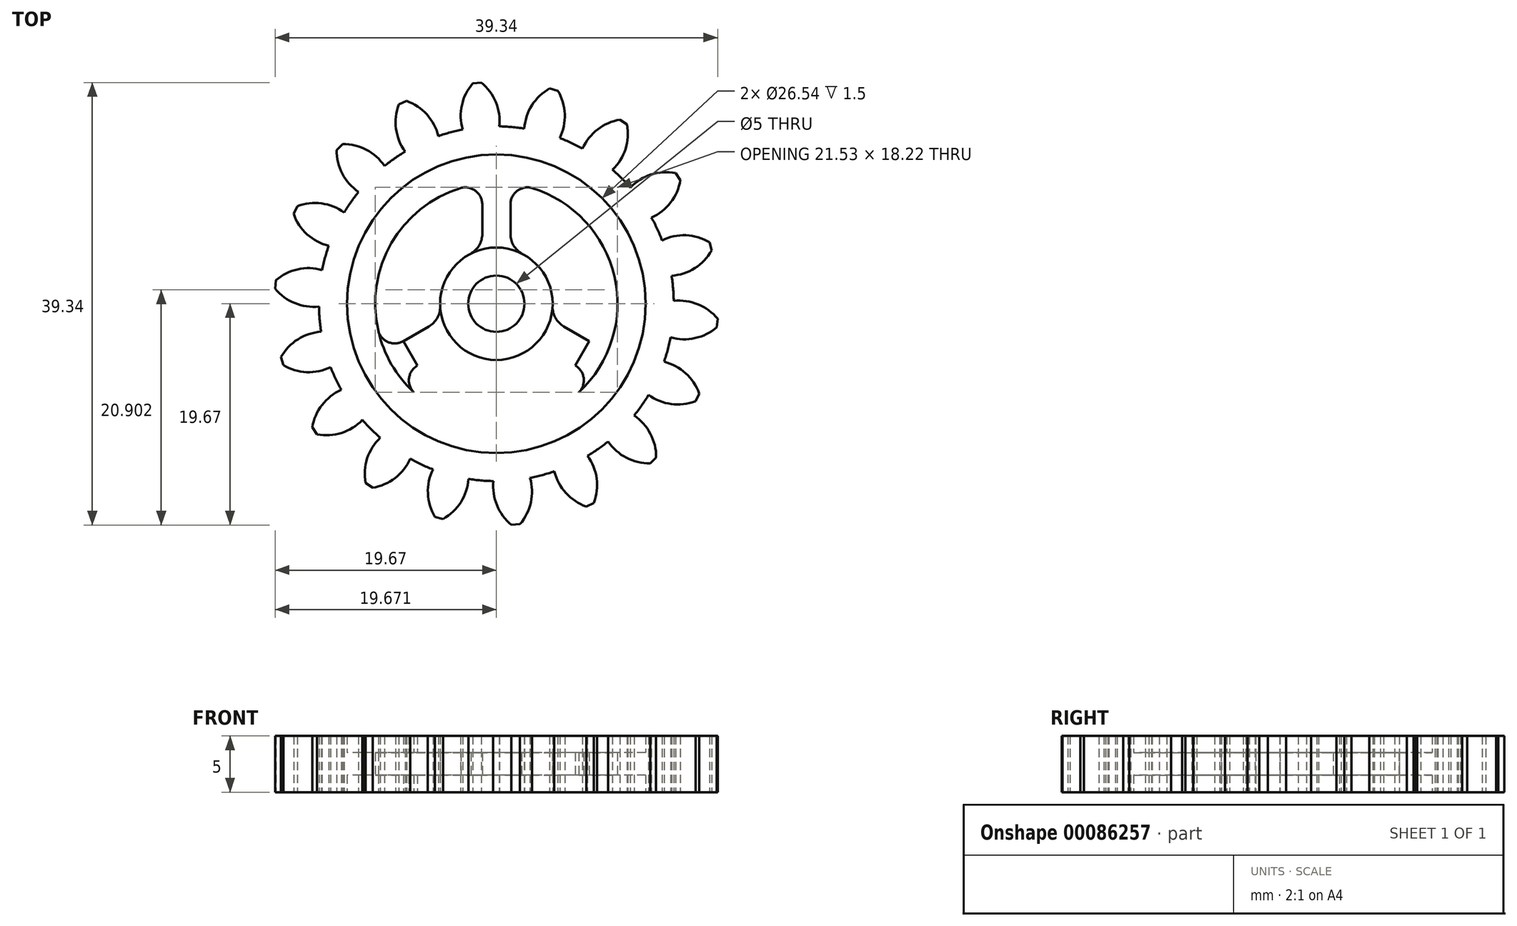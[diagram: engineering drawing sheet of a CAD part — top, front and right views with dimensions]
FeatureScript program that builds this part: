
annotation { "Feature Type Name" : "Feature", "Feature Type Description" : "" }
export const myFeature = defineFeature(function(context is Context, id is Id, definition is map)
    precondition{}
    {
        {
            assignVariable(context, id + "F0", {"name" : "Teeth", "anyValue" : 18});
        }
        {
            assignVariable(context, id + "F1", {"name" : "GearDepth", "anyValue" : 5});
        }
        {
            var Q0;
            Q0=qCreatedBy(makeId("Top.planeOp"),FACE);
            var sketch = newSketch(context, id + "F2", { "sketchPlane" : qUnion([Q0])});
            skCircle(sketch, "E0", {"center": v(0, 0) * mm, "radius": 15.77 * mm});
            skCircle(sketch, "E1", {"center": v(0, 0) * mm, "radius": 17.74 * mm, "construction": true});
            skCircle(sketch, "E2", {"center": v(0, 0) * mm, "radius": 19.71 * mm, "construction": true});
            skLineSegment(sketch, "E3", {"start": v(0, 0) * mm, "end": v(0, 17.6) * mm, "construction": true});
            skLineSegment(sketch, "E4", {"start": v(0, 0) * mm, "end": v(-1.57, 17.98) * mm, "construction": true});
            skLineSegment(sketch, "E5", {"start": v(0, 17.74) * mm, "end": v(-10.54, 17.74) * mm, "construction": true});
            skLineSegment(sketch, "E6", {"start": v(0, 17.74) * mm, "end": v(-10.3, 14) * mm, "construction": true});
            skCircle(sketch, "E7", {"center": v(0, 17.74) * mm, "radius": 4.44 * mm, "construction": true});
            skCircle(sketch, "E8", {"center": v(-4.17, 16.22) * mm, "radius": 4.44 * mm, "construction": true});
            skArc(sketch, "E9", {"start": v(-8.34, 17.74) * mm, "mid": v(-0.03, 14.63) * mm, "end": v(-8.28, 17.89) * mm, "construction": true});
            skArc(sketch, "E10.trimOffspring", {"start": v(0.26, 15.77) * mm, "mid": v(-0.05, 17.92) * mm, "end": v(-1.34, 19.67) * mm});
            skArc(sketch, "E11.MirrorCS", {"start": v(-3, 15.48) * mm, "mid": v(-3.06, 17.66) * mm, "end": v(-2.1, 19.6) * mm});
            skLineSegment(sketch, "E12", {"start": v(-2.1, 19.6) * mm, "end": v(-1.34, 19.67) * mm});
            skLineSegment(sketch, "E13.19.1", {"start": v(4.07, 19.29) * mm, "end": v(4.8, 19.12) * mm});
            skCircle(sketch, "E14", {"center": v(0, 0) * mm, "radius": 2.5 * mm});
            skSolve(sketch);
        }
        {
            var Q0;
            Q0=qCreatedBy(makeId("Front.planeOp"),FACE);
            var sketch = newSketch(context, id + "F3", { "sketchPlane" : qUnion([Q0])});
            skLineSegment(sketch, "E15", {"start": v(0, 0) * mm, "end": v(0, 61.57) * mm});
            skSolve(sketch);
        }
        {
            var Q0;
            {var subQ0=sQuery(id+"F2.wireOp",EDGE,"E10.trimOffspring");Q0=makeQuery(id+"F2.imprint","IMPRINT",FACE,{"disambiguationData":[TD([[makeQuery(id+"F2.imprint","IMPRINT",EDGE,{"derivedFrom":subQ0}),1.0]])]});}
            var Q1;
            {var subQ0=sQuery(id+"F2.wireOp",EDGE,"E0");var subQ1=makeQuery(id+"F2.imprint","INTERSECT",VERTEX,{"derivedFrom":[subQ0,sQuery(id+"F2.wireOp",EDGE,"E10.trimOffspring")]});Q1=makeQuery(id+"F2.imprint","IMPRINT",FACE,{"disambiguationData":[TD([[makeQuery(id+"F2.imprint","IMPRINT",EDGE,{"disambiguationData":[TD([[subQ1,-1.0]])],"derivedFrom":subQ0}),1.0]])]});}
            var Q2;
            {var subQ0=sQuery(id+"F2.wireOp",EDGE,"E13.1.0");Q2=makeQuery(id+"F2.imprint","IMPRINT",FACE,{"disambiguationData":[TD([[makeQuery(id+"F2.imprint","IMPRINT",EDGE,{"derivedFrom":subQ0}),1.0]])]});}
            var Q3;
            {var subQ0=sQuery(id+"F2.wireOp",EDGE,"E13.2.0");Q3=makeQuery(id+"F2.imprint","IMPRINT",FACE,{"disambiguationData":[TD([[makeQuery(id+"F2.imprint","IMPRINT",EDGE,{"derivedFrom":subQ0}),1.0]])]});}
            var Q4;
            {var subQ0=sQuery(id+"F2.wireOp",EDGE,"E13.3.0");Q4=makeQuery(id+"F2.imprint","IMPRINT",FACE,{"disambiguationData":[TD([[makeQuery(id+"F2.imprint","IMPRINT",EDGE,{"derivedFrom":subQ0}),1.0]])]});}
            var Q5;
            {var subQ0=sQuery(id+"F2.wireOp",EDGE,"E13.4.0");Q5=makeQuery(id+"F2.imprint","IMPRINT",FACE,{"disambiguationData":[TD([[makeQuery(id+"F2.imprint","IMPRINT",EDGE,{"derivedFrom":subQ0}),1.0]])]});}
            var Q6;
            {var subQ0=sQuery(id+"F2.wireOp",EDGE,"E13.5.0");Q6=makeQuery(id+"F2.imprint","IMPRINT",FACE,{"disambiguationData":[TD([[makeQuery(id+"F2.imprint","IMPRINT",EDGE,{"derivedFrom":subQ0}),1.0]])]});}
            var Q7;
            {var subQ0=sQuery(id+"F2.wireOp",EDGE,"E13.6.0");Q7=makeQuery(id+"F2.imprint","IMPRINT",FACE,{"disambiguationData":[TD([[makeQuery(id+"F2.imprint","IMPRINT",EDGE,{"derivedFrom":subQ0}),1.0]])]});}
            var Q8;
            {var subQ0=sQuery(id+"F2.wireOp",EDGE,"E13.7.0");Q8=makeQuery(id+"F2.imprint","IMPRINT",FACE,{"disambiguationData":[TD([[makeQuery(id+"F2.imprint","IMPRINT",EDGE,{"derivedFrom":subQ0}),1.0]])]});}
            var Q9;
            {var subQ0=sQuery(id+"F2.wireOp",EDGE,"E13.8.0");Q9=makeQuery(id+"F2.imprint","IMPRINT",FACE,{"disambiguationData":[TD([[makeQuery(id+"F2.imprint","IMPRINT",EDGE,{"derivedFrom":subQ0}),1.0]])]});}
            var Q10;
            {var subQ0=sQuery(id+"F2.wireOp",EDGE,"E13.9.0");Q10=makeQuery(id+"F2.imprint","IMPRINT",FACE,{"disambiguationData":[TD([[makeQuery(id+"F2.imprint","IMPRINT",EDGE,{"derivedFrom":subQ0}),1.0]])]});}
            var Q11;
            {var subQ0=sQuery(id+"F2.wireOp",EDGE,"E13.10.0");Q11=makeQuery(id+"F2.imprint","IMPRINT",FACE,{"disambiguationData":[TD([[makeQuery(id+"F2.imprint","IMPRINT",EDGE,{"derivedFrom":subQ0}),1.0]])]});}
            var Q12;
            {var subQ0=sQuery(id+"F2.wireOp",EDGE,"E13.11.0");Q12=makeQuery(id+"F2.imprint","IMPRINT",FACE,{"disambiguationData":[TD([[makeQuery(id+"F2.imprint","IMPRINT",EDGE,{"derivedFrom":subQ0}),1.0]])]});}
            var Q13;
            {var subQ0=sQuery(id+"F2.wireOp",EDGE,"E13.12.0");Q13=makeQuery(id+"F2.imprint","IMPRINT",FACE,{"disambiguationData":[TD([[makeQuery(id+"F2.imprint","IMPRINT",EDGE,{"derivedFrom":subQ0}),1.0]])]});}
            var Q14;
            {var subQ0=sQuery(id+"F2.wireOp",EDGE,"E13.13.0");Q14=makeQuery(id+"F2.imprint","IMPRINT",FACE,{"disambiguationData":[TD([[makeQuery(id+"F2.imprint","IMPRINT",EDGE,{"derivedFrom":subQ0}),1.0]])]});}
            var Q15;
            {var subQ0=sQuery(id+"F2.wireOp",EDGE,"E13.14.0");Q15=makeQuery(id+"F2.imprint","IMPRINT",FACE,{"disambiguationData":[TD([[makeQuery(id+"F2.imprint","IMPRINT",EDGE,{"derivedFrom":subQ0}),1.0]])]});}
            var Q16;
            {var subQ0=sQuery(id+"F2.wireOp",EDGE,"E13.15.0");Q16=makeQuery(id+"F2.imprint","IMPRINT",FACE,{"disambiguationData":[TD([[makeQuery(id+"F2.imprint","IMPRINT",EDGE,{"derivedFrom":subQ0}),1.0]])]});}
            var Q17;
            {var subQ0=sQuery(id+"F2.wireOp",EDGE,"E13.16.0");Q17=makeQuery(id+"F2.imprint","IMPRINT",FACE,{"disambiguationData":[TD([[makeQuery(id+"F2.imprint","IMPRINT",EDGE,{"derivedFrom":subQ0}),1.0]])]});}
            var Q18;
            {var subQ0=sQuery(id+"F2.wireOp",EDGE,"E13.17.0");Q18=makeQuery(id+"F2.imprint","IMPRINT",FACE,{"disambiguationData":[TD([[makeQuery(id+"F2.imprint","IMPRINT",EDGE,{"derivedFrom":subQ0}),1.0]])]});}
            var Q19;
            {var subQ0=sQuery(id+"F2.wireOp",EDGE,"E13.18.0");Q19=makeQuery(id+"F2.imprint","IMPRINT",FACE,{"disambiguationData":[TD([[makeQuery(id+"F2.imprint","IMPRINT",EDGE,{"derivedFrom":subQ0}),1.0]])]});}
            var Q20;
            {var subQ0=sQuery(id+"F2.wireOp",EDGE,"E13.19.0");Q20=makeQuery(id+"F2.imprint","IMPRINT",FACE,{"disambiguationData":[TD([[makeQuery(id+"F2.imprint","IMPRINT",EDGE,{"derivedFrom":subQ0}),1.0]])]});}
            var Q21;
            Q21=sQuery(id+"F2.wireOp",EDGE,"E0");
            var Q22;
            Q22=sQuery(id+"F2.wireOp",EDGE,"E10.trimOffspring");
            var Q23;
            Q23=sQuery(id+"F2.wireOp",EDGE,"E12");
            var Q24;
            Q24=sQuery(id+"F2.wireOp",EDGE,"E11.MirrorCS");
            extrude(context, id + "F4", {"entities" : qUnion([Q0, Q1, Q2, Q3, Q4, Q5, Q6, Q7, Q8, Q9, Q10, Q11, Q12, Q13, Q14, Q15, Q16, Q17, Q18, Q19, Q20]), "surfaceEntities" : qUnion([Q21, Q22, Q23, Q24]), "depth" : (getVariable(context, 'GearDepth')) * mm});
        }
        {
            var Q0;
            Q0=makeQuery(id+"F4.opExtrude","SWEPT_BODY",BODY,{"disambiguationData":[OSD([sQuery(id+"F2.wireOp",EDGE,"E0"),sQuery(id+"F2.wireOp",EDGE,"E10.trimOffspring"),sQuery(id+"F2.wireOp",EDGE,"E11.MirrorCS"),sQuery(id+"F2.wireOp",EDGE,"E12"),sQuery(id+"F2.wireOp",EDGE,"E14")])]});
            var Q1;
            Q1=sQuery(id+"F3.wireOp",EDGE,"E15");
            circularPattern(context, id + "F5", {"operationType" : NewBodyOperationType.ADD, "entities" : qUnion([Q0]), "axis" : qUnion([Q1]), "angle" : (360 / getVariable(context, 'Teeth')) * degree, "instanceCount" : getVariable(context, 'Teeth')});
        }
        {
            var Q0;
            Q0=qCreatedBy(makeId("Top.planeOp"),FACE);
            var sketch = newSketch(context, id + "F6", { "sketchPlane" : qUnion([Q0])});
            skCircle(sketch, "E16", {"center": v(0, 0) * mm, "radius": 5 * mm});
            skCircle(sketch, "E17", {"center": v(0, 0) * mm, "radius": 13.27 * mm});
            skLineSegment(sketch, "E18.bottom", {"start": v(-1.25, 8.82) * mm, "end": v(1.25, 8.82) * mm});
            skLineSegment(sketch, "E18.top", {"start": v(-1.25, 6.2) * mm, "end": v(1.25, 6.2) * mm});
            skLineSegment(sketch, "E18.left", {"start": v(-1.25, 8.82) * mm, "end": v(-1.25, 6.2) * mm});
            skLineSegment(sketch, "E18.right", {"start": v(1.25, 8.82) * mm, "end": v(1.25, 6.2) * mm});
            skLineSegment(sketch, "E19", {"start": v(0, 0) * mm, "end": v(0, 14.95) * mm, "construction": true});
            skArc(sketch, "E20", {"start": v(1.25, 6.2) * mm, "mid": v(1.52, 5.2) * mm, "end": v(2.26, 4.46) * mm});
            skArc(sketch, "E21.MirrorCS", {"start": v(-1.25, 6.2) * mm, "mid": v(-1.52, 5.2) * mm, "end": v(-2.26, 4.46) * mm});
            skCircle(sketch, "E22", {"center": v(0, 0) * mm, "radius": 10.77 * mm});
            skArc(sketch, "E23", {"start": v(-1.25, 8.82) * mm, "mid": v(-1.84, 10.02) * mm, "end": v(-3.15, 10.3) * mm});
            skArc(sketch, "E24.MirrorCS", {"start": v(1.25, 8.82) * mm, "mid": v(1.84, 10.02) * mm, "end": v(3.15, 10.3) * mm});
            skArc(sketch, "E25.1.0", {"start": v(7.01, -5.5) * mm, "mid": v(7.76, -6.6) * mm, "end": v(7.34, -7.88) * mm});
            skArc(sketch, "E25.1.1", {"start": v(8.26, -3.33) * mm, "mid": v(9.6, -3.42) * mm, "end": v(10.5, -2.42) * mm});
            skLineSegment(sketch, "E25.1.2", {"start": v(8.26, -3.33) * mm, "end": v(7.01, -5.5) * mm});
            skLineSegment(sketch, "E25.1.3", {"start": v(8.26, -3.33) * mm, "end": v(6, -2.02) * mm});
            skLineSegment(sketch, "E25.1.4", {"start": v(7.01, -5.5) * mm, "end": v(4.74, -4.18) * mm});
            skLineSegment(sketch, "E25.1.5", {"start": v(6, -2.02) * mm, "end": v(4.74, -4.18) * mm});
            skArc(sketch, "E25.1.6", {"start": v(4.74, -4.18) * mm, "mid": v(3.74, -3.91) * mm, "end": v(2.73, -4.19) * mm});
            skArc(sketch, "E25.1.7", {"start": v(6, -2.02) * mm, "mid": v(5.26, -1.28) * mm, "end": v(5, -0.27) * mm});
            skArc(sketch, "E25.2.0", {"start": v(-8.26, -3.33) * mm, "mid": v(-9.6, -3.42) * mm, "end": v(-10.5, -2.42) * mm});
            skArc(sketch, "E25.2.1", {"start": v(-7.01, -5.5) * mm, "mid": v(-7.76, -6.6) * mm, "end": v(-7.34, -7.88) * mm});
            skLineSegment(sketch, "E25.2.2", {"start": v(-7.01, -5.5) * mm, "end": v(-8.26, -3.33) * mm});
            skLineSegment(sketch, "E25.2.3", {"start": v(-7.01, -5.5) * mm, "end": v(-4.74, -4.18) * mm});
            skLineSegment(sketch, "E25.2.4", {"start": v(-8.26, -3.33) * mm, "end": v(-6, -2.02) * mm});
            skLineSegment(sketch, "E25.2.5", {"start": v(-4.74, -4.18) * mm, "end": v(-6, -2.02) * mm});
            skArc(sketch, "E25.2.6", {"start": v(-6, -2.02) * mm, "mid": v(-5.26, -1.28) * mm, "end": v(-5, -0.27) * mm});
            skArc(sketch, "E25.2.7", {"start": v(-4.74, -4.18) * mm, "mid": v(-3.74, -3.91) * mm, "end": v(-2.73, -4.19) * mm});
            skLineSegment(sketch, "E25.anchor1", {"start": v(0, 0) * mm, "end": v(1.25, 8.82) * mm, "construction": true});
            skLineSegment(sketch, "E25.anchor2", {"start": v(0, 0) * mm, "end": v(-8.26, -3.33) * mm, "construction": true});
            skSolve(sketch);
        }
        {
            var Q0;
            Q0=makeQuery(id+"F6.imprint","IMPRINT",FACE,{"disambiguationData":[TD([[makeQuery(id+"F6.imprint","IMPRINT",EDGE,{"derivedFrom":sQuery(id+"F6.wireOp",EDGE,"E18.right")}),1.0]])]});
            var Q1;
            Q1=makeQuery(id+"F6.imprint","IMPRINT",FACE,{"disambiguationData":[TD([[makeQuery(id+"F6.imprint","IMPRINT",EDGE,{"derivedFrom":sQuery(id+"F6.wireOp",EDGE,"E18.left")}),-1.0]])]});
            var Q2;
            {var subQ0=sQuery(id+"F6.wireOp",EDGE,"275d905c-acd0-4467-9c6b-4b6f0fef50b3.1.1");Q2=makeQuery(id+"F6.imprint","IMPRINT",FACE,{"disambiguationData":[TD([[makeQuery(id+"F6.imprint","IMPRINT",EDGE,{"derivedFrom":subQ0}),1.0]])]});}
            extrude(context, id + "F7", {"entities" : qUnion([Q0, Q1, Q2]), "operationType" : NewBodyOperationType.REMOVE, "endBound" : BoundingType.THROUGH_ALL, "depth" : 25 * mm});
        }
        {
            var Q0;
            Q0=makeQuery(id+"F6.imprint","IMPRINT",FACE,{"disambiguationData":[TD([[makeQuery(id+"F6.imprint","IMPRINT",EDGE,{"derivedFrom":sQuery(id+"F6.wireOp",EDGE,"E17")}),1.0]])]});
            var Q1;
            {var subQ0=sQuery(id+"F6.wireOp",EDGE,"E16");var subQ5=makeQuery(id+"F6.imprint","INTERSECT",VERTEX,{"derivedFrom":[subQ0,sQuery(id+"F6.wireOp",EDGE,"E20")]});Q1=makeQuery(id+"F6.imprint","IMPRINT",FACE,{"disambiguationData":[TD([[makeQuery(id+"F6.imprint","IMPRINT",EDGE,{"disambiguationData":[TD([[subQ5,-1.0]])],"derivedFrom":subQ0}),1.0]])]});}
            var Q2;
            Q2=makeQuery(id+"F6.imprint","IMPRINT",FACE,{"disambiguationData":[TD([[makeQuery(id+"F6.imprint","IMPRINT",EDGE,{"derivedFrom":sQuery(id+"F6.wireOp",EDGE,"E18.top")}),-1.0]])]});
            var Q3;
            Q3=makeQuery(id+"F6.imprint","IMPRINT",FACE,{"disambiguationData":[TD([[makeQuery(id+"F6.imprint","IMPRINT",EDGE,{"derivedFrom":sQuery(id+"F6.wireOp",EDGE,"E18.bottom")}),-1.0]])]});
            var Q4;
            Q4=makeQuery(id+"F6.imprint","IMPRINT",FACE,{"disambiguationData":[TD([[makeQuery(id+"F6.imprint","IMPRINT",EDGE,{"derivedFrom":sQuery(id+"F6.wireOp",EDGE,"E18.bottom")}),1.0]])]});
            var Q5;
            Q5=makeQuery(id+"F6.imprint","IMPRINT",FACE,{"disambiguationData":[TD([[makeQuery(id+"F6.imprint","IMPRINT",EDGE,{"derivedFrom":sQuery(id+"F6.wireOp",EDGE,"E25.2.5")}),-1.0]])]});
            var Q6;
            Q6=makeQuery(id+"F6.imprint","IMPRINT",FACE,{"disambiguationData":[TD([[makeQuery(id+"F6.imprint","IMPRINT",EDGE,{"derivedFrom":sQuery(id+"F6.wireOp",EDGE,"E25.2.2")}),-1.0]])]});
            var Q7;
            {var subQ0=sQuery(id+"F6.wireOp",EDGE,"E25.2.0");Q7=makeQuery(id+"F6.imprint","IMPRINT",FACE,{"disambiguationData":[TD([[makeQuery(id+"F6.imprint","IMPRINT",EDGE,{"derivedFrom":subQ0}),1.0]])]});}
            var Q8;
            {var subQ0=sQuery(id+"F6.wireOp",EDGE,"E25.1.0");Q8=makeQuery(id+"F6.imprint","IMPRINT",FACE,{"disambiguationData":[TD([[makeQuery(id+"F6.imprint","IMPRINT",EDGE,{"derivedFrom":subQ0}),1.0]])]});}
            var Q9;
            Q9=makeQuery(id+"F6.imprint","IMPRINT",FACE,{"disambiguationData":[TD([[makeQuery(id+"F6.imprint","IMPRINT",EDGE,{"derivedFrom":sQuery(id+"F6.wireOp",EDGE,"E25.1.2")}),-1.0]])]});
            var Q10;
            Q10=makeQuery(id+"F6.imprint","IMPRINT",FACE,{"disambiguationData":[TD([[makeQuery(id+"F6.imprint","IMPRINT",EDGE,{"derivedFrom":sQuery(id+"F6.wireOp",EDGE,"E25.1.5")}),-1.0]])]});
            extrude(context, id + "F8", {"entities" : qUnion([Q0, Q1, Q2, Q3, Q4, Q5, Q6, Q7, Q8, Q9, Q10]), "operationType" : NewBodyOperationType.REMOVE, "depth" : 1.5 * mm});
        }
        {
            var Q0;
            {var subQ0=sQuery(id+"F6.wireOp",EDGE,"E25.1.0");var subQ6=makeQuery(id+"F4.opExtrude","CAP_FACE",FACE,{"disambiguationData":[OSD([sQuery(id+"F2.wireOp",EDGE,"E0"),sQuery(id+"F2.wireOp",EDGE,"E10.trimOffspring"),sQuery(id+"F2.wireOp",EDGE,"E11.MirrorCS"),sQuery(id+"F2.wireOp",EDGE,"E12"),sQuery(id+"F2.wireOp",EDGE,"E14")])],"isStart":true});Q0=makeQuery(id+"F8.boolean.opBoolean","SPLIT",FACE,{"disambiguationData":[TD([makeQuery(id+"F8.opExtrude","SWEPT_FACE",FACE,{"disambiguationData":[OSD([subQ0])]})])],"derivedFrom":makeQuery(id+"F5.boolean.opBoolean","MERGE",FACE,{"derivedFrom":[subQ6,makeQuery(id+"F5.opPattern","COPY",FACE,{"derivedFrom":subQ6,"instanceName":"1"}),makeQuery(id+"F5.opPattern","COPY",FACE,{"derivedFrom":subQ6,"instanceName":"2"}),makeQuery(id+"F5.opPattern","COPY",FACE,{"derivedFrom":subQ6,"instanceName":"3"}),makeQuery(id+"F5.opPattern","COPY",FACE,{"derivedFrom":subQ6,"instanceName":"4"}),makeQuery(id+"F5.opPattern","COPY",FACE,{"derivedFrom":subQ6,"instanceName":"5"}),makeQuery(id+"F5.opPattern","COPY",FACE,{"derivedFrom":subQ6,"instanceName":"6"}),makeQuery(id+"F5.opPattern","COPY",FACE,{"derivedFrom":subQ6,"instanceName":"7"}),makeQuery(id+"F5.opPattern","COPY",FACE,{"derivedFrom":subQ6,"instanceName":"8"}),makeQuery(id+"F5.opPattern","COPY",FACE,{"derivedFrom":subQ6,"instanceName":"9"}),makeQuery(id+"F5.opPattern","COPY",FACE,{"derivedFrom":subQ6,"instanceName":"10"}),makeQuery(id+"F5.opPattern","COPY",FACE,{"derivedFrom":subQ6,"instanceName":"11"}),makeQuery(id+"F5.opPattern","COPY",FACE,{"derivedFrom":subQ6,"instanceName":"12"}),makeQuery(id+"F5.opPattern","COPY",FACE,{"derivedFrom":subQ6,"instanceName":"13"}),makeQuery(id+"F5.opPattern","COPY",FACE,{"derivedFrom":subQ6,"instanceName":"14"}),makeQuery(id+"F5.opPattern","COPY",FACE,{"derivedFrom":subQ6,"instanceName":"15"}),makeQuery(id+"F5.opPattern","COPY",FACE,{"derivedFrom":subQ6,"instanceName":"16"}),makeQuery(id+"F5.opPattern","COPY",FACE,{"derivedFrom":subQ6,"instanceName":"17"})]})});}
            extrude(context, id + "F9", {"entities" : qUnion([Q0]), "operationType" : NewBodyOperationType.REMOVE, "endBound" : BoundingType.THROUGH_ALL, "oppositeDirection" : true, "depth" : 25 * mm});
        }
        {
            var Q0;
            Q0=makeQuery(id+"F6.imprint","IMPRINT",FACE,{"disambiguationData":[TD([[makeQuery(id+"F6.imprint","IMPRINT",EDGE,{"derivedFrom":sQuery(id+"F6.wireOp",EDGE,"E17")}),1.0]])]});
            var Q1;
            {var subQ0=sQuery(id+"F6.wireOp",EDGE,"E16");var subQ5=makeQuery(id+"F6.imprint","INTERSECT",VERTEX,{"derivedFrom":[subQ0,sQuery(id+"F6.wireOp",EDGE,"E20")]});Q1=makeQuery(id+"F6.imprint","IMPRINT",FACE,{"disambiguationData":[TD([[makeQuery(id+"F6.imprint","IMPRINT",EDGE,{"disambiguationData":[TD([[subQ5,-1.0]])],"derivedFrom":subQ0}),1.0]])]});}
            var Q2;
            {var subQ0=sQuery(id+"F6.wireOp",EDGE,"E25.1.0");Q2=makeQuery(id+"F6.imprint","IMPRINT",FACE,{"disambiguationData":[TD([[makeQuery(id+"F6.imprint","IMPRINT",EDGE,{"derivedFrom":subQ0}),1.0]])]});}
            var Q3;
            Q3=makeQuery(id+"F6.imprint","IMPRINT",FACE,{"disambiguationData":[TD([[makeQuery(id+"F6.imprint","IMPRINT",EDGE,{"derivedFrom":sQuery(id+"F6.wireOp",EDGE,"E25.1.2")}),-1.0]])]});
            var Q4;
            Q4=makeQuery(id+"F6.imprint","IMPRINT",FACE,{"disambiguationData":[TD([[makeQuery(id+"F6.imprint","IMPRINT",EDGE,{"derivedFrom":sQuery(id+"F6.wireOp",EDGE,"E25.1.5")}),-1.0]])]});
            var Q5;
            Q5=makeQuery(id+"F6.imprint","IMPRINT",FACE,{"disambiguationData":[TD([[makeQuery(id+"F6.imprint","IMPRINT",EDGE,{"derivedFrom":sQuery(id+"F6.wireOp",EDGE,"E18.top")}),-1.0]])]});
            var Q6;
            Q6=makeQuery(id+"F6.imprint","IMPRINT",FACE,{"disambiguationData":[TD([[makeQuery(id+"F6.imprint","IMPRINT",EDGE,{"derivedFrom":sQuery(id+"F6.wireOp",EDGE,"E18.bottom")}),-1.0]])]});
            var Q7;
            Q7=makeQuery(id+"F6.imprint","IMPRINT",FACE,{"disambiguationData":[TD([[makeQuery(id+"F6.imprint","IMPRINT",EDGE,{"derivedFrom":sQuery(id+"F6.wireOp",EDGE,"E18.bottom")}),1.0]])]});
            var Q8;
            Q8=makeQuery(id+"F6.imprint","IMPRINT",FACE,{"disambiguationData":[TD([[makeQuery(id+"F6.imprint","IMPRINT",EDGE,{"derivedFrom":sQuery(id+"F6.wireOp",EDGE,"E25.2.5")}),-1.0]])]});
            var Q9;
            Q9=makeQuery(id+"F6.imprint","IMPRINT",FACE,{"disambiguationData":[TD([[makeQuery(id+"F6.imprint","IMPRINT",EDGE,{"derivedFrom":sQuery(id+"F6.wireOp",EDGE,"E25.2.2")}),-1.0]])]});
            var Q10;
            {var subQ0=sQuery(id+"F6.wireOp",EDGE,"E25.2.0");Q10=makeQuery(id+"F6.imprint","IMPRINT",FACE,{"disambiguationData":[TD([[makeQuery(id+"F6.imprint","IMPRINT",EDGE,{"derivedFrom":subQ0}),1.0]])]});}
            extrude(context, id + "F10", {"entities" : qUnion([Q0, Q1, Q2, Q3, Q4, Q5, Q6, Q7, Q8, Q9, Q10]), "operationType" : NewBodyOperationType.REMOVE, "depth" : 5 * mm, "hasSecondDirection" : true, "secondDirectionOppositeDirection" : false, "secondDirectionDepth" : 3.5 * mm});
        }
        {
            var Q0;
            Q0=qCreatedBy(makeId("Top.planeOp"),FACE);
            var sketch = newSketch(context, id + "F11", { "sketchPlane" : qUnion([Q0])});
            skCircle(sketch, "E26", {"center": v(0, 0) * mm, "radius": 2.5 * mm});
            skCircle(sketch, "E27", {"center": v(0, 0) * mm, "radius": 5 * mm});
            skSolve(sketch);
        }
        {
            var Q0;
            Q0=makeQuery(id+"F11.imprint","IMPRINT",FACE,{"disambiguationData":[TD([[makeQuery(id+"F11.imprint","IMPRINT",EDGE,{"derivedFrom":sQuery(id+"F11.wireOp",EDGE,"E26")}),-1.0]])]});
            extrude(context, id + "F12", {"entities" : qUnion([Q0]), "operationType" : NewBodyOperationType.ADD, "depth" : 5 * mm});
        }
    });
